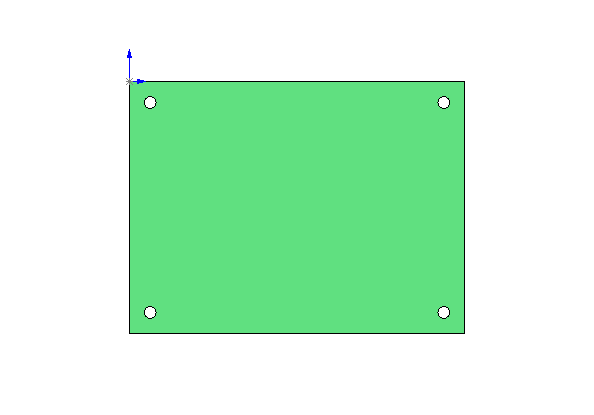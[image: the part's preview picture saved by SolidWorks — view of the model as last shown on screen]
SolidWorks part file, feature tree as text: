
SOLIDWORKS PART (.sldprt)
format: sldprt  version: not decoded by parser v0  size: 114,176 bytes
history: native  units: mm
features: sketch x2, material x1, extrude x1, cut_extrude x1, pattern_linear x1 (+13 scaffold rows collapsed)
feature tree (19):
  scaffold x13  (default folders/planes/origin — collapsed)
  material  "Material <not specified>"
  sketch  "Sketch1"  dims[D1=101.6mm D2=76.2mm]
  extrude  "Extrude1"  Depth=1.6002mm
  sketch  "Sketch2"  dims[D1=3.556mm D2=6.35mm D3=6.35mm]
  cut_extrude  "Cut-Extrude1"  Depth=1.6002mm
  pattern_linear  "LPattern1"  Count1=2 Count2=2 Spacing1=63.5mm Spacing2=88.9mm
decode coverage: 5 of 5 modeling features carry decoded parameters
note: suppression state not decoded; provenance and decode notes live in map.json
